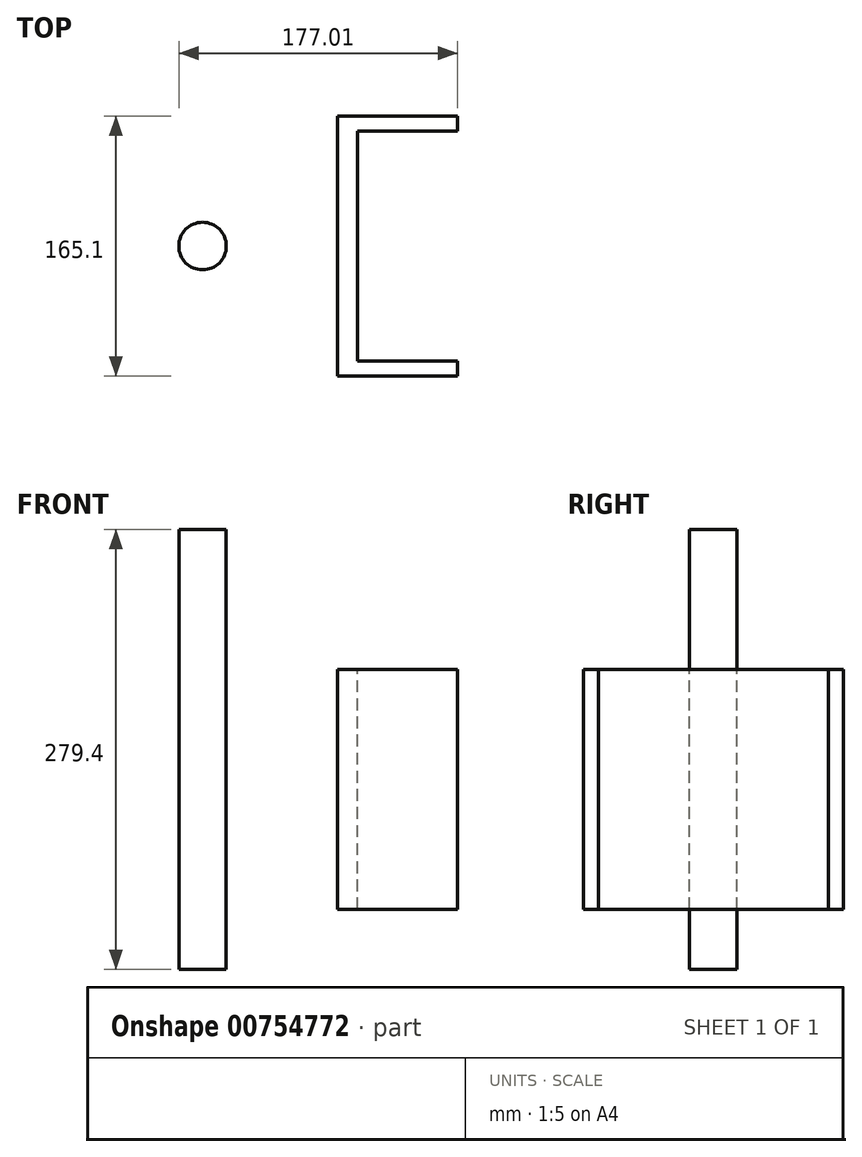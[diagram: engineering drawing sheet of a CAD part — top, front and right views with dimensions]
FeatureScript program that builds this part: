
annotation { "Feature Type Name" : "Feature", "Feature Type Description" : "" }
export const myFeature = defineFeature(function(context is Context, id is Id, definition is map)
    precondition{}
    {
        {
            var Q0;
            Q0=qCreatedBy(makeId("Right.planeOp"),FACE);
            cPlane(context, id + "F0", {"entities" : qUnion([Q0]), "cplaneType" : CPlaneType.OFFSET, "offset" : 254 * mm, "width" : 152.4 * mm, "height" : 152.4 * mm});
        }
        {
            var Q0;
            Q0=qCreatedBy(id+"F0.planeOp",FACE);
            var sketch = newSketch(context, id + "F1", { "sketchPlane" : qUnion([Q0])});
            skLineSegment(sketch, "E0.bottom", {"start": v(-82.55, 76.2) * mm, "end": v(82.55, 76.2) * mm});
            skLineSegment(sketch, "E0.top", {"start": v(-82.55, -76.2) * mm, "end": v(82.55, -76.2) * mm});
            skLineSegment(sketch, "E0.left", {"start": v(-82.55, 76.2) * mm, "end": v(-82.55, -76.2) * mm});
            skLineSegment(sketch, "E0.right", {"start": v(82.55, 76.2) * mm, "end": v(82.55, -76.2) * mm});
            skSolve(sketch);
        }
        {
            var Q0;
            Q0=qSketchRegion(id+"F1",true);
            extrude(context, id + "F2", {"entities" : qUnion([Q0]), "oppositeDirection" : true, "depth" : 12.7 * mm, "offsetDistance" : 25.4 * mm, "hasSecondDirection" : true, "secondDirectionOppositeDirection" : false, "secondDirectionDepth" : 63.5 * mm});
        }
        {
            var Q0;
            Q0=makeQuery(id+"F2.opExtrude","SWEPT_FACE",FACE,{"disambiguationData":[OSD([sQuery(id+"F1.wireOp",EDGE,"E0.bottom")])]});
            var sketch = newSketch(context, id + "F3", { "sketchPlane" : qUnion([Q0])});
            skCircle(sketch, "E1", {"center": v(155.58, 0) * mm, "radius": 15.08 * mm});
            skSolve(sketch);
        }
        {
            var Q0;
            Q0=qSketchRegion(id+"F3",true);
            extrude(context, id + "F4", {"entities" : qUnion([Q0]), "oppositeDirection" : true, "depth" : 190.5 * mm, "offsetDistance" : 25.4 * mm, "hasSecondDirection" : true, "secondDirectionOppositeDirection" : false, "secondDirectionDepth" : 88.9 * mm});
        }
        {
            var Q0;
            Q0=makeQuery(id+"F2.opExtrude","SWEPT_FACE",FACE,{"disambiguationData":[OSD([sQuery(id+"F1.wireOp",EDGE,"E0.bottom")])]});
            var sketch = newSketch(context, id + "F5", { "sketchPlane" : qUnion([Q0])});
            skLineSegment(sketch, "E2.bottom", {"start": v(317.5, -73.03) * mm, "end": v(254, -73.03) * mm});
            skLineSegment(sketch, "E2.top", {"start": v(317.5, 73.03) * mm, "end": v(254, 73.02) * mm});
            skLineSegment(sketch, "E2.left", {"start": v(317.5, -73.03) * mm, "end": v(317.5, 73.03) * mm});
            skLineSegment(sketch, "E2.right", {"start": v(254, -73.03) * mm, "end": v(254, 73.03) * mm});
            skSolve(sketch);
        }
        {
            var Q0;
            Q0=qSketchRegion(id+"F5",true);
            extrude(context, id + "F6", {"entities" : qUnion([Q0]), "operationType" : NewBodyOperationType.REMOVE, "endBound" : BoundingType.THROUGH_ALL, "oppositeDirection" : true, "depth" : 25.4 * mm, "offsetDistance" : 25.4 * mm});
        }
    });
